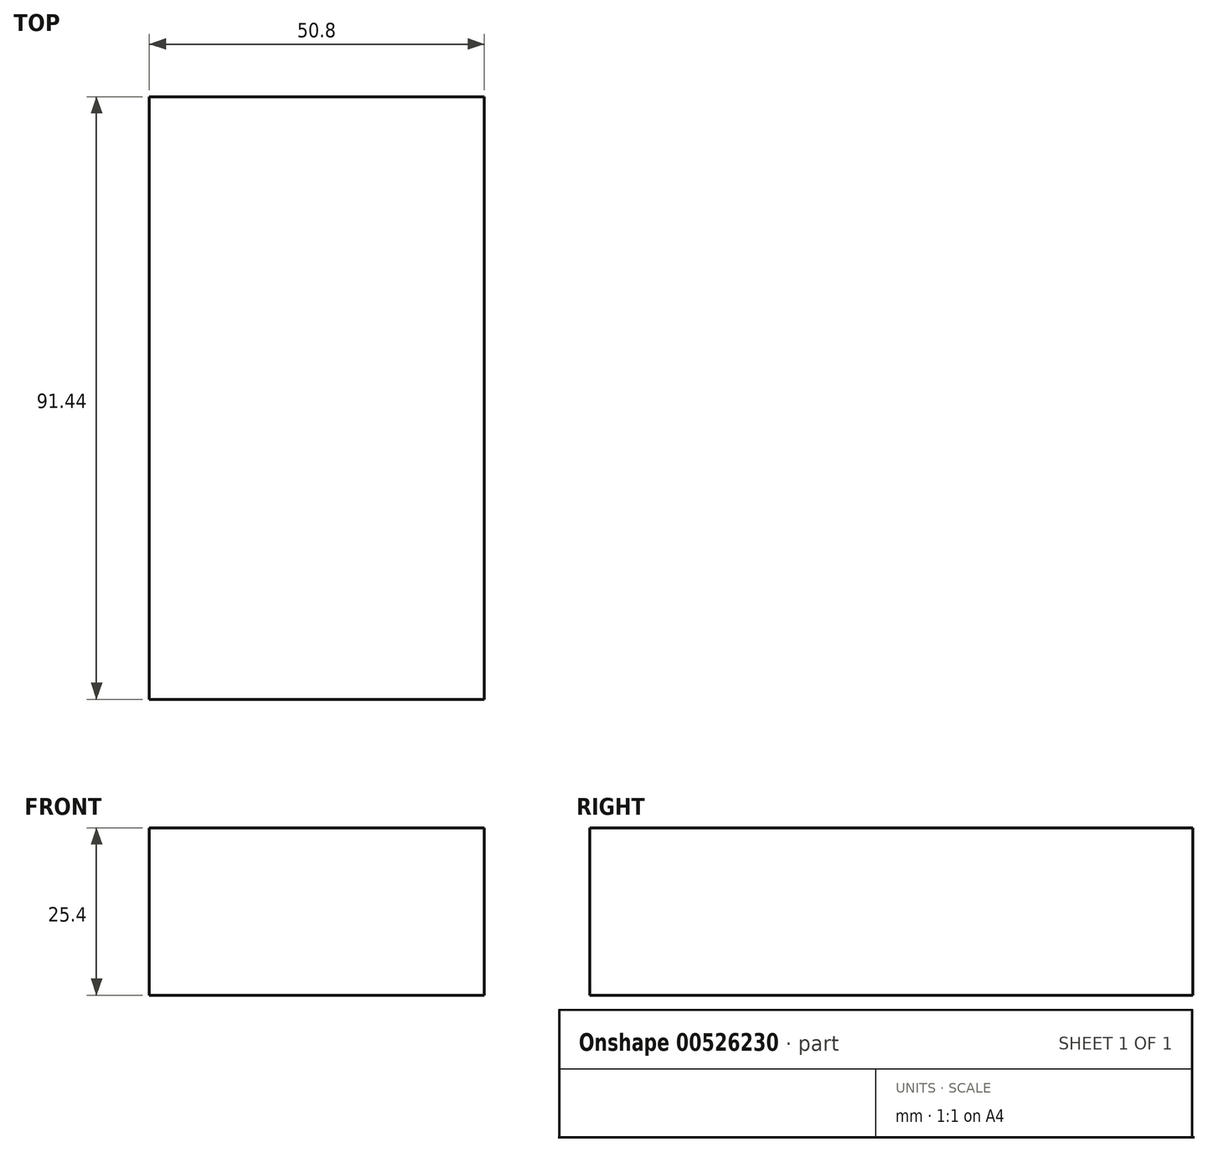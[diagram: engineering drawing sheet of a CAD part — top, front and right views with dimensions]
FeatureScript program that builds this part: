
annotation { "Feature Type Name" : "Feature", "Feature Type Description" : "" }
export const myFeature = defineFeature(function(context is Context, id is Id, definition is map)
    precondition{}
    {
        {
            var Q0;
            Q0=qCreatedBy(makeId("Top.planeOp"),FACE);
            var sketch = newSketch(context, id + "F0", { "sketchPlane" : qUnion([Q0])});
            skLineSegment(sketch, "E0.bottom", {"start": v(25.4, 45.72) * mm, "end": v(-25.4, 45.72) * mm});
            skLineSegment(sketch, "E0.top", {"start": v(25.4, -45.72) * mm, "end": v(-25.4, -45.72) * mm});
            skLineSegment(sketch, "E0.left", {"start": v(25.4, 45.72) * mm, "end": v(25.4, -45.72) * mm});
            skLineSegment(sketch, "E0.right", {"start": v(-25.4, 45.72) * mm, "end": v(-25.4, -45.72) * mm});
            skPoint(sketch, "E0.middle", {"position": v(0, 0) * mm});
            skSolve(sketch);
        }
        {
            var Q0;
            Q0=makeQuery(id+"F0.imprint","IMPRINT",FACE,{"disambiguationData":[TD([[makeQuery(id+"F0.imprint","IMPRINT",EDGE,{"derivedFrom":sQuery(id+"F0.wireOp",EDGE,"E0.bottom")}),1.0]])]});
            extrude(context, id + "F1", {"entities" : qUnion([Q0]), "depth" : 25.4 * mm, "offsetDistance" : 25.4 * mm});
        }
    });
